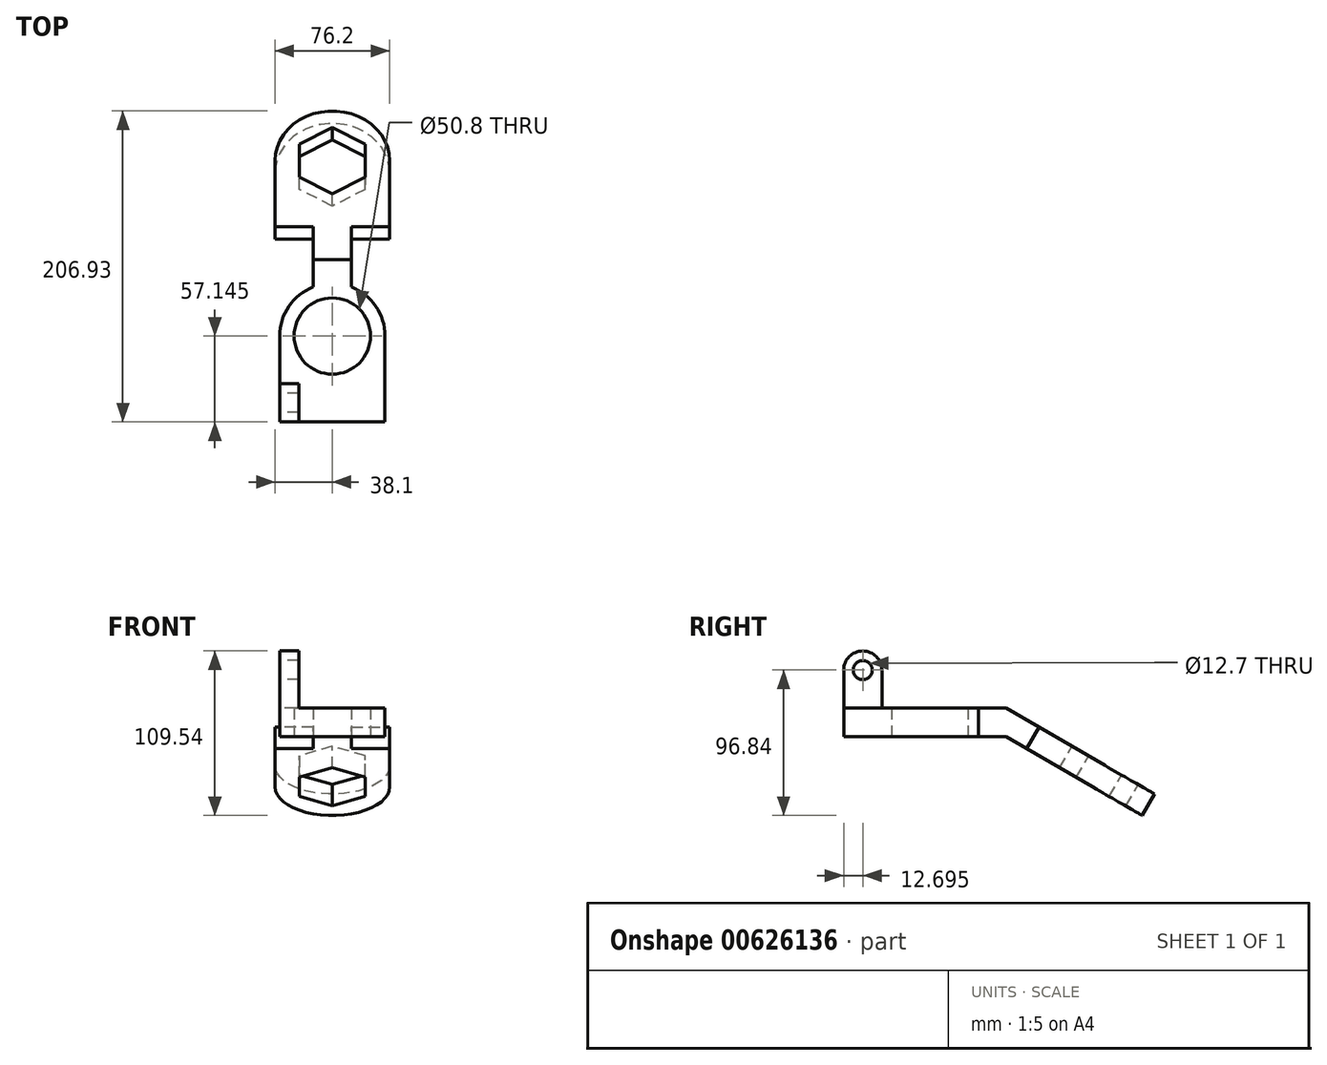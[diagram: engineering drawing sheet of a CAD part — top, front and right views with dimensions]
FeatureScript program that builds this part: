
annotation { "Feature Type Name" : "Feature", "Feature Type Description" : "" }
export const myFeature = defineFeature(function(context is Context, id is Id, definition is map)
    precondition{}
    {
        {
            var Q0;
            Q0=qCreatedBy(makeId("Top.planeOp"),FACE);
            var sketch = newSketch(context, id + "F0", { "sketchPlane" : qUnion([Q0])});
            skLineSegment(sketch, "E0.top", {"start": v(35.05, -28.58) * mm, "end": v(-35.05, -28.58) * mm});
            skLineSegment(sketch, "E0.left", {"start": v(35.05, 28.58) * mm, "end": v(35.05, -28.58) * mm});
            skLineSegment(sketch, "E0.right", {"start": v(-35.05, 28.58) * mm, "end": v(-35.05, -28.58) * mm});
            skPoint(sketch, "E0.middle", {"position": v(0, 0) * mm});
            skArc(sketch, "E1", {"start": v(35.05, 28.58) * mm, "mid": v(28.93, 48.37) * mm, "end": v(12.7, 61.25) * mm});
            skCircle(sketch, "E2", {"center": v(0, 28.58) * mm, "radius": 25.4 * mm});
            skLineSegment(sketch, "E3", {"start": v(12.7, 79.38) * mm, "end": v(12.7, 61.25) * mm});
            skLineSegment(sketch, "E4", {"start": v(-12.7, 61.25) * mm, "end": v(-12.7, 79.38) * mm});
            skLineSegment(sketch, "E5", {"start": v(-12.7, 79.38) * mm, "end": v(12.7, 79.38) * mm});
            skArc(sketch, "E6.trimOffspring", {"start": v(-12.7, 61.25) * mm, "mid": v(-28.93, 48.37) * mm, "end": v(-35.05, 28.58) * mm});
            skSolve(sketch);
        }
        {
            var Q0;
            Q0 = qSketchRegion(id + "F0", true);
            extrude(context, id + "F1", {"entities" : qUnion([Q0]), "depth" : 19.05 * mm, "offsetDistance" : 25.4 * mm});
        }
        {
            var Q0;
            Q0=makeQuery(id+"F1.opExtrude","SWEPT_FACE",FACE,{"disambiguationData":[OSD([sQuery(id+"F0.wireOp",EDGE,"E0.right")])]});
            var sketch = newSketch(context, id + "F2", { "sketchPlane" : qUnion([Q0])});
            skLineSegment(sketch, "E7.bottom", {"start": v(28.58, 19.05) * mm, "end": v(3.18, 19.05) * mm});
            skLineSegment(sketch, "E7.left", {"start": v(28.58, 19.05) * mm, "end": v(28.58, 44.45) * mm});
            skLineSegment(sketch, "E7.right", {"start": v(3.18, 19.05) * mm, "end": v(3.18, 44.45) * mm});
            skArc(sketch, "E8", {"start": v(28.58, 44.45) * mm, "mid": v(15.88, 57.15) * mm, "end": v(3.18, 44.45) * mm});
            skCircle(sketch, "E9", {"center": v(15.88, 44.45) * mm, "radius": 6.35 * mm});
            skSolve(sketch);
        }
        {
            var Q0;
            Q0 = qSketchRegion(id + "F2", true);
            extrude(context, id + "F3", {"entities" : qUnion([Q0]), "operationType" : NewBodyOperationType.ADD, "oppositeDirection" : true, "depth" : 12.7 * mm, "offsetDistance" : 25.4 * mm});
        }
        {
            var Q0;
            Q0=makeQuery(id+"F1.opExtrude","SWEPT_FACE",FACE,{"disambiguationData":[OSD([sQuery(id+"F0.wireOp",EDGE,"E4")])]});
            var sketch = newSketch(context, id + "F4", { "sketchPlane" : qUnion([Q0])});
            skLineSegment(sketch, "E10", {"start": v(-79.38, 19.05) * mm, "end": v(-178.36, -38.1) * mm});
            skLineSegment(sketch, "E11", {"start": v(-178.36, -38.1) * mm, "end": v(-170.11, -52.39) * mm});
            skLineSegment(sketch, "E12", {"start": v(-170.11, -52.39) * mm, "end": v(-79.38, 0) * mm});
            skSolve(sketch);
        }
        {
            var Q0;
            Q0=makeQuery(id+"F4.imprint","IMPRINT",FACE,{"disambiguationData":[TD([[makeQuery(id+"F4.imprint","IMPRINT",EDGE,{"derivedFrom":sQuery(id+"F4.wireOp",EDGE,"E10")}),1.0]])]});
            extrude(context, id + "F5", {"entities" : qUnion([Q0]), "operationType" : NewBodyOperationType.ADD, "depth" : 25.4 * mm, "offsetDistance" : 25.4 * mm, "hasSecondDirection" : true, "secondDirectionOppositeDirection" : true, "secondDirectionDepth" : 50.8 * mm});
        }
        {
            var Q0;
            Q0=makeQuery(id+"F5.opExtrude","SWEPT_FACE",FACE,{"disambiguationData":[OSD([sQuery(id+"F4.wireOp",EDGE,"E10")])]});
            var sketch = newSketch(context, id + "F6", { "sketchPlane" : qUnion([Q0])});
            skLineSegment(sketch, "E13", {"start": v(12.7, 59.22) * mm, "end": v(12.7, 84.62) * mm});
            skLineSegment(sketch, "E14", {"start": v(12.7, 84.62) * mm, "end": v(38.1, 84.62) * mm});
            skLineSegment(sketch, "E15", {"start": v(38.1, 84.62) * mm, "end": v(38.1, 59.22) * mm});
            skLineSegment(sketch, "E16", {"start": v(38.1, 59.22) * mm, "end": v(12.7, 59.22) * mm});
            skLineSegment(sketch, "E17", {"start": v(-12.7, 59.22) * mm, "end": v(-12.7, 84.62) * mm});
            skLineSegment(sketch, "E18", {"start": v(-12.7, 84.62) * mm, "end": v(-38.1, 84.62) * mm});
            skLineSegment(sketch, "E19", {"start": v(-38.1, 84.62) * mm, "end": v(-38.1, 59.22) * mm});
            skLineSegment(sketch, "E20", {"start": v(-38.1, 59.22) * mm, "end": v(-12.7, 59.22) * mm});
            skArc(sketch, "E21", {"start": v(38.1, 135.42) * mm, "mid": v(0, 173.52) * mm, "end": v(-38.1, 135.42) * mm});
            skPoint(sketch, "E21.centerSnap0", {"position": v(0, 59.22) * mm});
            skLineSegment(sketch, "E22", {"start": v(38.1, 135.42) * mm, "end": v(38.1, 173.52) * mm});
            skLineSegment(sketch, "E23", {"start": v(38.1, 173.52) * mm, "end": v(0, 173.52) * mm});
            skLineSegment(sketch, "E24", {"start": v(0, 173.52) * mm, "end": v(-38.1, 173.52) * mm});
            skLineSegment(sketch, "E25", {"start": v(-38.1, 173.52) * mm, "end": v(-38.1, 135.42) * mm});
            skSolve(sketch);
        }
        {
            var Q0;
            Q0 = qSketchRegion(id + "F6", true);
            extrude(context, id + "F7", {"entities" : qUnion([Q0]), "operationType" : NewBodyOperationType.REMOVE, "oppositeDirection" : true, "depth" : 25.4 * mm, "offsetDistance" : 25.4 * mm});
        }
        {
            var Q0;
            Q0=makeQuery(id+"F5.opExtrude","SWEPT_FACE",FACE,{"disambiguationData":[OSD([sQuery(id+"F4.wireOp",EDGE,"E10")])]});
            var sketch = newSketch(context, id + "F8", { "sketchPlane" : qUnion([Q0])});
            skCircle(sketch, "E26.cCircle", {"center": v(0, 135.42) * mm, "radius": 22 * mm, "construction": true});
            skLineSegment(sketch, "E26.0", {"start": v(0, 160.82) * mm, "end": v(22, 148.12) * mm});
            skLineSegment(sketch, "E26.1", {"start": v(22, 148.12) * mm, "end": v(22, 122.72) * mm});
            skLineSegment(sketch, "E26.2", {"start": v(22, 122.72) * mm, "end": v(0, 110.02) * mm});
            skLineSegment(sketch, "E26.3", {"start": v(0, 110.02) * mm, "end": v(-22, 122.72) * mm});
            skLineSegment(sketch, "E26.4", {"start": v(-22, 122.72) * mm, "end": v(-22, 148.12) * mm});
            skLineSegment(sketch, "E26.5", {"start": v(-22, 148.12) * mm, "end": v(0, 160.82) * mm});
            skPoint(sketch, "E26.0.midPoint", {"position": v(11, 154.47) * mm});
            skSolve(sketch);
        }
        {
            var Q0;
            Q0 = qSketchRegion(id + "F8", true);
            extrude(context, id + "F9", {"entities" : qUnion([Q0]), "operationType" : NewBodyOperationType.REMOVE, "endBound" : BoundingType.THROUGH_ALL, "oppositeDirection" : true, "depth" : 25.4 * mm, "offsetDistance" : 25.4 * mm});
        }
    });
